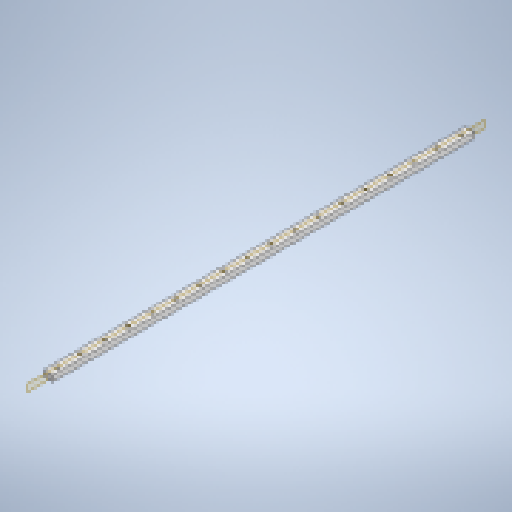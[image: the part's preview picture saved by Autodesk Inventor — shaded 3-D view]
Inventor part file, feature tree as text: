
AUTODESK INVENTOR PART (.ipt)
format: ipt  version: 2023 (Build 270158000, 158)  size: 183,296 bytes
history: native  units: mm
features: sketch x2, extrude x1, plane x1, revolve x1, pattern_linear x1
ambient origin geometry x8: Origin, YZ Plane, XZ Plane, XY Plane, X Axis, Y Axis, Z Axis, Center Point
bodies: Solid1 (feature_tree)
feature tree (6):
  extrude  "Extrusion1"  Depth=10.0mm
  plane  "Work Plane1"
  revolve  "Revolution1"  [1 undecoded]
  pattern_linear  "Rectangular Pattern1"  Spacing1=6.0mm  [1 undecoded]
  sketch  "Sketch1"  dims[d0=15.0mm d1=10.0mm]
  sketch  "Sketch4"  dims[d2=710.0mm d3=0.0mm d5=-7.5mm d6=6.0mm d7=3.5mm d8=4.5mm d9=15.0mm d10=360.0deg d11=200.0mm d13=40.0mm]
note: 2 required parameter values undecoded (feature->parameter linkage not recoverable at this tier; creation-order binding heuristic only, values carry confidence <= 0.55)